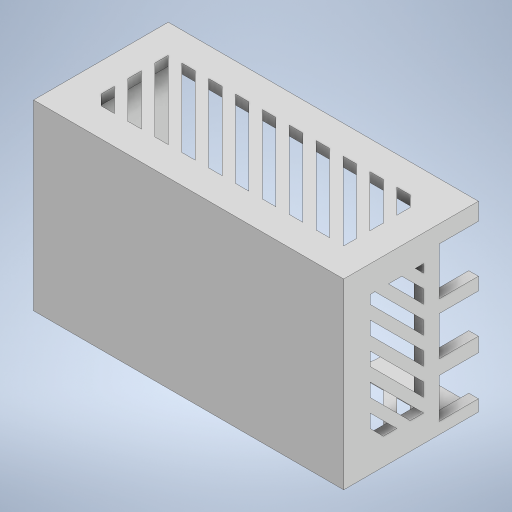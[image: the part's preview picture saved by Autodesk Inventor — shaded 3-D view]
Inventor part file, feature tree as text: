
AUTODESK INVENTOR PART (.ipt)
format: ipt  version: 2024 (Build 280153000, 153)  size: 580,608 bytes
history: native  units: in
note: dims shown in document units (in); Inventor stores cm internally (conversion verified against a paired STEP export)
features: sketch x9, extrude x8, projected_geometry x8, fillet x3
ambient origin geometry x8: Origin, YZ Plane, XZ Plane, XY Plane, X Axis, Y Axis, Z Axis, Center Point
bodies: Solid1 (feature_tree)
feature tree (28):
  sketch  "Sketch1"  dims[d0=1.5748in d1=0.0in d2=1.0598in d3=0.0in]
  extrude  "Extrusion1"  Depth=1.0598in TaperAngle=0.0deg
  extrude  "Extrusion2"  Depth=0.125in
  extrude  "Extrusion4"  Depth=0.06in
  fillet  "Fillet2"  Radius=0.03in
  extrude  "Extrusion5"  Depth=0.1969in TaperAngle=0.0deg
  fillet  "Fillet3"  Radius=0.6in
  fillet  "Fillet4"  [1 undecoded]
  extrude  "Extrusion6"  Depth=0.125in
  extrude  "Extrusion7"  Depth=0.125in
  extrude  "Extrusion8"  Depth=0.125in
  extrude  "Extrusion9"  Depth=0.125in
  sketch  "Sketch12"  dims[d29=0.125in d30=0.125in d31=0.125in d32=0.125in d33=0.125in d34=0.125in d35=0.125in d36=0.125in d37=0.125in d38=0.125in d39=0.125in d40=0.125in d41=0.125in d42=0.125in d43=0.125in d44=0.125in d45=0.0in d46=0.0in d61=0.35in d62=0.15in d63=135.0deg d64=0.125in d65=0.125in d66=0.125in d67=0.125in d68=0.125in d69=0.125in d70=0.125in d71=0.125in d72=0.125in d73=0.125in d74=0.125in d75=0.125in d76=0.125in d77=0.125in d78=0.125in d79=0.125in d80=0.125in d81=0.125in d82=1.0in d83=0.0in d84=0.5in d85=0.0344in d86=0.5in d87=0.0344in]
  sketch  "Sketch3"  dims[d8=1.3088in d9=0.0in d10=0.125in]
  projected_geometry  "Projected Loop1"
  projected_geometry  "Projected Loop2"
  projected_geometry  "Projected Loop3"
  projected_geometry  "Projected Loop4"
  projected_geometry  "Projected Loop5"
  projected_geometry  "Projected Loop6"
  sketch  "Sketch6"  dims[d11=1.4508in d12=0.0in d13=0.06in d14=0.03in]
  sketch  "Sketch7"  dims[d15=0.0787in d16=0.0in d17=0.1969in d18=0.0in d19=0.6in d20=45.0deg]
  sketch  "Sketch8"  dims[d21=0.125in d22=0.125in]
  sketch  "Sketch9"  dims[d23=0.125in d24=0.125in]
  projected_geometry  "Projected Loop7"
  sketch  "Sketch10"  dims[d25=0.125in d26=0.125in]
  projected_geometry  "Projected Loop8"
  sketch  "Sketch11"  dims[d27=0.125in d28=0.125in]
note: 1 required parameter value undecoded (feature->parameter linkage not recoverable at this tier; creation-order binding heuristic only, values carry confidence <= 0.55)
